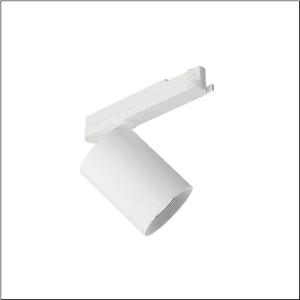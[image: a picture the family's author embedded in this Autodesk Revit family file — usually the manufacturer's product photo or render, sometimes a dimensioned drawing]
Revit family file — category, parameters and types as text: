
# Revit family: spot_21_51se13mbb5b
name_source: partatom
category: Lighting Fixtures
units: mm (PartAtom-declared; Revit-internal decimal feet)

## family parameters
Cut with Voids When Loaded = No
Host = Face
Light Source = No
Part Type = Normal
Room Calculation Point = No
Round Connector Dimension = Use Diameter
Shared = No

## types (1)
- --- (1 x LED, 5350 lm, 41.8 W, 3000K)
    Apparent Load = 42 VA
    CIE Flux Codes = 95 98 99 100 100
    Color Rendering = 90
    Color Temperature = 3000K
    Default Elevation = 1800 mm
    Description = Spot 21, directional spotlight, light control with lens, of PMMA, LED rated luminous flux: 5.140lm, light colour: 930, control gear: ECG Multilumen, with 3-phase adapter, mains connection: 220..240V, AC, 50/60Hz, of aluminium, traffic white (RAL 9016), length: 213mm, diameter: 105mm, protection rating (complete): IP20, insulation class (complete): insulation class I (protective earthing), certification: CE, impact resistance: IK02, permissible ambient temperature for indoor applications: -20..+40°C, packaging unit: 1 piece
    Height = 175 mm
    Lamp = 1 x LED
    Lamp Light Flux = 5350 lm
    Lamp Power = 41.8 W
    Lamp count = 1
    Length = 105 mm
    Luminous efficacy = 128 lm/W
    Manufacturer = Siteco
    ModVariant = No
    Model = 51SE13MBB5B
    Mounting Place = Ceiling
    Mounting Type = Pendant
    Number of Poles = 1
    OnlyDefault = Yes
    Power Factor = 1
    Product Name = Spot 21
    Product group = directional spotlight
    ProductGroupID = 905
    Protection Class = Protection class I
    Protection Degree = IP 20
    RLX_Detail_Level = 1
    RLX_Emergency_Light_Flux = 0 lm
    RLX_Emergency_Type = 0
    RLX_Emergency_Type_DB = No
    RlxData = <blob elided: 17661 chars, md5=1f96db5e>
    Socket = socket
    Standby Power = 0 W
    System Light Flux = 5350 lm
    System Power = 42 W
    Type Comments = factory setting: luminous flux: 100 % | (ON | ON | ON | ON) | 1050 mA
    Type Image = l_1003976.jpg
    URL = http://relux.com
    VarID = @adj_075733
    Voltage = 0 V
    Weight = 0.00 kg
    Width = 0 mm  [stored 0 ft]

note: [stored X ft] marks values corroborated as IEEE doubles in the binary element streams (Revit-internal decimal feet)

## geometry (parser evidence)
native form markers: Blend x4, Sweep x11
no freeform markers — native parametric forms only
